# Revit family: MaviGard Cloche d'Alarme Incendie
name_source: partatom
category: Fire Alarm Devices
units: mm (PartAtom-declared; Revit-internal decimal feet)

## family parameters
Cut with Voids When Loaded = No
Host = Face
Maintain Annotation Orientation = Yes
OmniClass Number = 23.85.30.21
OmniClass Title = Environmental Detection/Registration
Part Type = Normal
Room Calculation Point = No
Round Connector Dimension = Use Diameter
Shared = No

## types (1)
- MaviGard Cloche d'alarme Incendie Conventionnelle
    Adresse ligne 1 = Şerifali Mahallesi Kutup Sokak No:27/1-2-4 Ümraniye TR-34775 İSTANBUL
    Code de  Performance = EN 54-3
    Code de Produit = MG-5400
    Cost = 0 $
    Couleur = Rouge
    Default Elevation = 0 mm  [stored 0 ft]
    Description = Cloche d'alarme Incendie
    Deuxime Matèriel = Mètale
    Durée de la garantie Travail = 2
    Durée de la garantie réservé = 2
    Hauteur Nominale = 150 mm
    Hauteur de Montage = Hauteur 2,4 m du sol
    Largeur Nominale = 55 mm
    Longeur Nominale = 150 mm
    Manuel d'installation = https://mavilielektronik.com
    Manufacturer = Mavili Elektronik Ticaret A.Ş.
    Matériel Principe = Mètale Rouge
    Model = MaviGard
    Numèro de Fax = (+)90 216 466 45 10
    Numéro de pose des travaux publics = 833-598
    Poids = 610 gr
    Surface de Montage = Montage à Mur
    Tempèrature de Fonctionnement = (-10°C) - (+55°C)
    URL = https://www.mavili.com.tr
    Unité de durée de garantie = Ans
    Voltage de fonctionnement (default) = 24 V/DC
    protection de Classe = IP 51
    voltage fonction d'opération = 18-33V/DC

note: [stored X ft] marks values corroborated as IEEE doubles in the binary element streams (Revit-internal decimal feet)

## geometry (parser evidence)
native form markers: Sweep x3
no freeform markers — native parametric forms only
